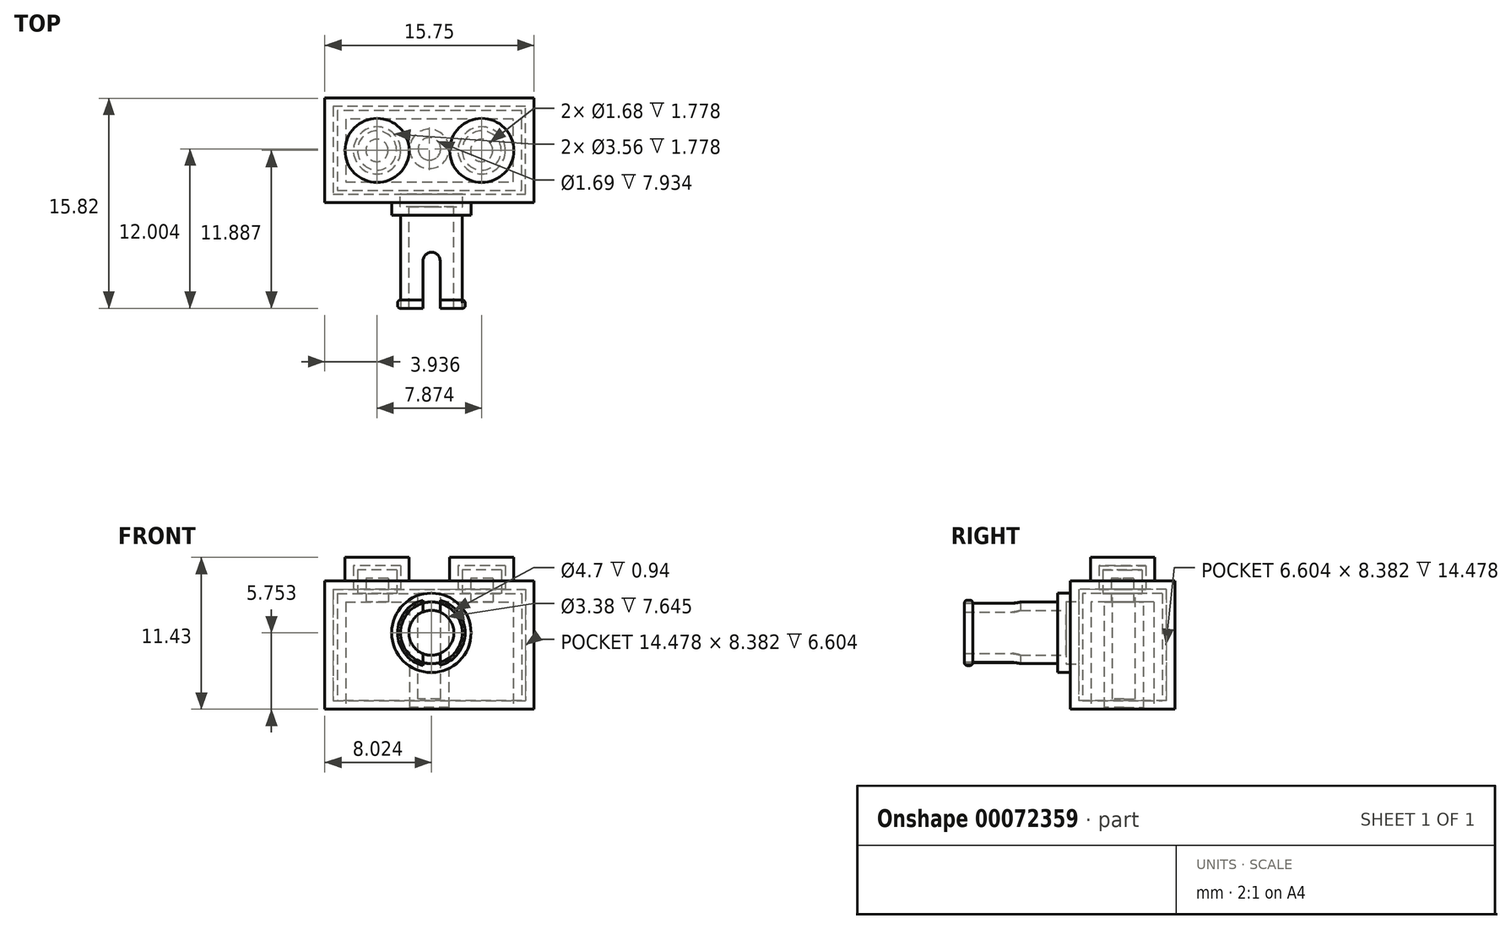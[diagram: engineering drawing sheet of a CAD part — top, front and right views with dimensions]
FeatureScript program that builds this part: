
annotation { "Feature Type Name" : "Feature", "Feature Type Description" : "" }
export const myFeature = defineFeature(function(context is Context, id is Id, definition is map)
    precondition{}
    {
        {
            var Q0;
            Q0=qCreatedBy(makeId("Top.planeOp"),FACE);
            var sketch = newSketch(context, id + "F0", { "sketchPlane" : qUnion([Q0])});
            skLineSegment(sketch, "E0", {"start": v(0, 0) * mm, "end": v(15.75, 0) * mm});
            skLineSegment(sketch, "E1", {"start": v(15.75, 0) * mm, "end": v(15.75, 7.87) * mm});
            skLineSegment(sketch, "E2", {"start": v(15.75, 7.87) * mm, "end": v(0, 7.87) * mm});
            skLineSegment(sketch, "E3", {"start": v(0, 7.87) * mm, "end": v(0, 0) * mm});
            skSolve(sketch);
        }
        {
            var Q0;
            Q0=makeQuery(id+"F0.imprint","IMPRINT",FACE,{"disambiguationData":[TD([[makeQuery(id+"F0.imprint","IMPRINT",EDGE,{"derivedFrom":sQuery(id+"F0.wireOp",EDGE,"E0")}),1.0]])]});
            extrude(context, id + "F1", {"entities" : qUnion([Q0]), "depth" : 9.65 * mm});
        }
        {
            var Q0;
            Q0=makeQuery(id+"F1.opExtrude","CAP_FACE",FACE,{"disambiguationData":[OSD([sQuery(id+"F0.wireOp",EDGE,"E0"),sQuery(id+"F0.wireOp",EDGE,"E1"),sQuery(id+"F0.wireOp",EDGE,"E2"),sQuery(id+"F0.wireOp",EDGE,"E3")])],"isStart":false});
            var sketch = newSketch(context, id + "F2", { "sketchPlane" : qUnion([Q0])});
            skCircle(sketch, "E4", {"center": v(3.94, 3.94) * mm, "radius": 2.41 * mm});
            skCircle(sketch, "E5", {"center": v(11.8, 3.94) * mm, "radius": 2.41 * mm});
            skSolve(sketch);
        }
        {
            var Q0;
            Q0=makeQuery(id+"F2.imprint","IMPRINT",FACE,{"disambiguationData":[TD([[makeQuery(id+"F2.imprint","IMPRINT",EDGE,{"derivedFrom":sQuery(id+"F2.wireOp",EDGE,"E4")}),1.0]])]});
            extrude(context, id + "F3", {"entities" : qUnion([Q0]), "operationType" : NewBodyOperationType.ADD, "depth" : 1.78 * mm});
        }
        {
            var Q0;
            Q0=makeQuery(id+"F2.imprint","IMPRINT",FACE,{"disambiguationData":[TD([[makeQuery(id+"F2.imprint","IMPRINT",EDGE,{"derivedFrom":sQuery(id+"F2.wireOp",EDGE,"E5")}),1.0]])]});
            extrude(context, id + "F4", {"entities" : qUnion([Q0]), "operationType" : NewBodyOperationType.ADD, "depth" : 1.78 * mm});
        }
        {
            var Q0;
            Q0=makeQuery(id+"F1.opExtrude","CAP_FACE",FACE,{"disambiguationData":[OSD([sQuery(id+"F0.wireOp",EDGE,"E0"),sQuery(id+"F0.wireOp",EDGE,"E1"),sQuery(id+"F0.wireOp",EDGE,"E2"),sQuery(id+"F0.wireOp",EDGE,"E3")])],"isStart":true});
            shell(context, id + "F5", {"entities" : qUnion([Q0]), "thickness" : 1.57 * mm});
        }
        {
            var Q0;
            Q0=makeQuery(id+"F5.opShell","OFFSET_FACE",FACE,{"disambiguationData":[OSD([sQuery(id+"F0.wireOp",EDGE,"E0"),sQuery(id+"F0.wireOp",EDGE,"E1"),sQuery(id+"F0.wireOp",EDGE,"E2"),sQuery(id+"F0.wireOp",EDGE,"E3")])]});
            var sketch = newSketch(context, id + "F6", { "sketchPlane" : qUnion([Q0])});
            skCircle(sketch, "E6", {"center": v(7.87, -4.05) * mm, "radius": 1.48 * mm});
            skPoint(sketch, "E6.centerSnap0", {"position": v(7.87, -6.3) * mm});
            skSolve(sketch);
        }
        {
            var Q0;
            Q0=makeQuery(id+"F6.imprint","IMPRINT",FACE,{"disambiguationData":[TD([[makeQuery(id+"F6.imprint","IMPRINT",EDGE,{"derivedFrom":sQuery(id+"F6.wireOp",EDGE,"E6")}),1.0]])]});
            extrude(context, id + "F7", {"entities" : qUnion([Q0]), "operationType" : NewBodyOperationType.ADD, "depth" : 7.93 * mm});
        }
        {
            var Q0;
            Q0=qCreatedBy(makeId("Front.planeOp"),FACE);
            var sketch = newSketch(context, id + "F8", { "sketchPlane" : qUnion([Q0])});
            skCircle(sketch, "E7", {"center": v(8.02, 5.75) * mm, "radius": 2.98 * mm});
            skSolve(sketch);
        }
        {
            var Q0;
            Q0=makeQuery(id+"F8.imprint","IMPRINT",FACE,{"disambiguationData":[TD([[makeQuery(id+"F8.imprint","IMPRINT",EDGE,{"derivedFrom":sQuery(id+"F8.wireOp",EDGE,"E7")}),1.0]])]});
            extrude(context, id + "F9", {"entities" : qUnion([Q0]), "operationType" : NewBodyOperationType.ADD, "depth" : 0.94 * mm});
        }
        {
            var Q0;
            Q0=makeQuery(id+"F9.opExtrude","CAP_FACE",FACE,{"disambiguationData":[OSD([sQuery(id+"F8.wireOp",EDGE,"E7")])],"isStart":false});
            var sketch = newSketch(context, id + "F10", { "sketchPlane" : qUnion([Q0])});
            skCircle(sketch, "E8", {"center": v(8.02, 5.75) * mm, "radius": 2.32 * mm});
            skSolve(sketch);
        }
        {
            var Q0;
            Q0=makeQuery(id+"F10.imprint","IMPRINT",FACE,{"disambiguationData":[TD([[makeQuery(id+"F10.imprint","IMPRINT",EDGE,{"derivedFrom":sQuery(id+"F10.wireOp",EDGE,"E8")}),1.0]])]});
            extrude(context, id + "F11", {"entities" : qUnion([Q0]), "operationType" : NewBodyOperationType.ADD, "depth" : 7 * mm});
        }
        {
            var Q0;
            Q0=makeQuery(id+"F11.opExtrude","CAP_FACE",FACE,{"disambiguationData":[OSD([sQuery(id+"F10.wireOp",EDGE,"E8")])],"isStart":false});
            var sketch = newSketch(context, id + "F12", { "sketchPlane" : qUnion([Q0])});
            skCircle(sketch, "E9", {"center": v(8.02, 5.75) * mm, "radius": 2.54 * mm});
            skSolve(sketch);
        }
        {
            var Q0;
            Q0=makeQuery(id+"F12.imprint","IMPRINT",FACE,{"disambiguationData":[TD([[makeQuery(id+"F12.imprint","IMPRINT",EDGE,{"derivedFrom":sQuery(id+"F12.wireOp",EDGE,"E9")}),1.0]])]});
            extrude(context, id + "F13", {"entities" : qUnion([Q0]), "oppositeDirection" : true, "depth" : 0.64 * mm});
        }
        {
            var Q0;
            Q0=makeQuery(id+"F13.opExtrude","CAP_EDGE",EDGE,{"disambiguationData":[OSD([sQuery(id+"F12.wireOp",EDGE,"E9")])],"isStart":true});
            fillet(context, id + "F14", {"entities" : qUnion([Q0]), "radius" : 0.2 * mm, "tangentPropagation" : true, "allowEdgeOverflow" : false});
        }
        {
            var Q0;
            Q0=makeQuery(id+"F13.opExtrude","CAP_EDGE",EDGE,{"disambiguationData":[OSD([sQuery(id+"F12.wireOp",EDGE,"E9")])],"isStart":false});
            fillet(context, id + "F15", {"entities" : qUnion([Q0]), "radius" : 0.23 * mm, "tangentPropagation" : true, "allowEdgeOverflow" : false});
        }
        {
            var Q0;
            Q0=makeQuery(id+"F11.opExtrude","CAP_FACE",FACE,{"disambiguationData":[OSD([sQuery(id+"F10.wireOp",EDGE,"E8")])],"isStart":false});
            shell(context, id + "F16", {"entities" : qUnion([Q0]), "thickness" : 0.64 * mm});
        }
        {
            var Q0;
            Q0=qCreatedBy(makeId("Top.planeOp"),FACE);
            var sketch = newSketch(context, id + "F17", { "sketchPlane" : qUnion([Q0])});
            skCircle(sketch, "E10", {"center": v(8.04, -4.37) * mm, "radius": 0.64 * mm});
            skLineSegment(sketch, "E11.rect.bottom", {"start": v(8.68, -4.37) * mm, "end": v(7.4, -4.37) * mm});
            skLineSegment(sketch, "E11.rect.top", {"start": v(8.68, -8.04) * mm, "end": v(7.4, -8.04) * mm});
            skLineSegment(sketch, "E11.rect.left", {"start": v(8.68, -4.37) * mm, "end": v(8.68, -8.04) * mm});
            skLineSegment(sketch, "E11.rect.right", {"start": v(7.4, -4.37) * mm, "end": v(7.4, -8.04) * mm});
            skPoint(sketch, "E11.rect.middle", {"position": v(8.04, -6.2) * mm});
            skSolve(sketch);
        }
        {
            var Q0;
            Q0=makeQuery(id+"F17.imprint","IMPRINT",FACE,{"disambiguationData":[TD([[makeQuery(id+"F17.imprint","IMPRINT",EDGE,{"derivedFrom":sQuery(id+"F17.wireOp",EDGE,"E11.rect.top")}),-1.0]])]});
            var Q1;
            {var subQ0=sQuery(id+"F17.wireOp",EDGE,"E11.rect.bottom");Q1=makeQuery(id+"F17.imprint","IMPRINT",FACE,{"disambiguationData":[TD([[makeQuery(id+"F17.imprint","IMPRINT",EDGE,{"derivedFrom":subQ0}),-1.0]])]});}
            var Q2;
            {var subQ0=sQuery(id+"F17.wireOp",EDGE,"E11.rect.bottom");Q2=makeQuery(id+"F17.imprint","IMPRINT",FACE,{"disambiguationData":[TD([[makeQuery(id+"F17.imprint","IMPRINT",EDGE,{"derivedFrom":subQ0}),1.0]])]});}
            extrude(context, id + "F18", {"entities" : qUnion([Q0, Q1, Q2]), "operationType" : NewBodyOperationType.REMOVE, "depth" : 12.3 * mm});
        }
    });
